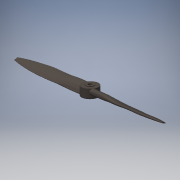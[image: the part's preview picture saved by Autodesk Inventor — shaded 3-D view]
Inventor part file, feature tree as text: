
AUTODESK INVENTOR PART (.ipt)
format: ipt  version: 2018 (Build 220112000, 112)  size: 1,668,608 bytes
history: native  units: mm
features: sketch x9, plane x7, other x4, revolve x1, loft x1, fillet x1, pattern_circular x1, direct_edit x1
ambient origin geometry x8: Origin, YZ Plane, XZ Plane, XY Plane, X Axis, Y Axis, Z Axis, Center Point
bodies: Solid1 (feature_tree)
feature tree (25):
  revolve  "Revolution1"  [1 undecoded]
  plane  "Work Plane1"
  plane  "Work Plane2"
  plane  "Work Plane3"
  plane  "Work Plane4"
  plane  "Work Plane5"
  plane  "Work Plane6"
  sketch  "Sketch2"  dims[d2=3.0mm d3=1.5mm d4=22.0mm]
  sketch  "Sketch3"  dims[d5=2.0mm]
  sketch  "Sketch4"  dims[d6=1.5mm]
  sketch  "Sketch5"  dims[d7=1.5mm]
  sketch  "Sketch6"  dims[d8=90.0deg]
  sketch  "Sketch7"  dims[d9=56.14mm d10=96.77mm d11=126.14mm d12=157.8mm d13=189.33mm d14=220.0mm d20=40.0mm]
  plane  "Work Plane7"
  sketch  "Sketch8"  dims[d24=33.278655mm]
  loft  "Loft1"
  fillet  "Fillet1"  Radius=22.0mm
  other  "Work Axis1"
  pattern_circular  "Circular Pattern1"  Count=4  [1 undecoded]
  direct_edit  "Direct Edit1"
  sketch  "Sketch1"  dims[d0=5.0mm d1=20.0mm]
  other  "Image1"
  sketch  "Sketch10"  dims[d76=8.695358mm d84=13.02mm d85=15.153mm d86=15.153mm d87=13.012mm d88=9.821mm d95=13.02mm d96=15.153mm d97=15.153mm d98=13.012mm d99=9.821mm d100=221.460376mm d102=176.089529mm d131=13.02mm d132=10.0mm d135=15.153mm d136=10.0mm d142=10.0mm d143=15.153mm d150=13.012mm d151=10.0mm d152=9.821mm d153=10.0mm d154=12.0mm d155=0.0mm d156=90.0deg d157=0.0mm d158=90.0deg d159=0.0mm d160=90.0deg d161=0.0mm d162=90.0deg d163=0.0mm d164=90.0deg d165=0.0mm d166=90.0deg d167=0.0mm d168=90.0deg d169=2.0mm d170=2.0mm d171=2.0mm d172=7.436mm d173=2.0mm d174=7.969mm d175=2.0mm d176=5.859mm d177=2.0mm d178=0.313mm d179=2.0mm d180=8.125mm d181=2.0mm d182=9.277mm d183=2.0mm d184=1.18mm d185=20.0mm d186=360.0deg d189=20.0mm]
  other  "Work Axis2"
  other  "Size1"
note: 2 required parameter values undecoded (feature->parameter linkage not recoverable at this tier; creation-order binding heuristic only, values carry confidence <= 0.55)